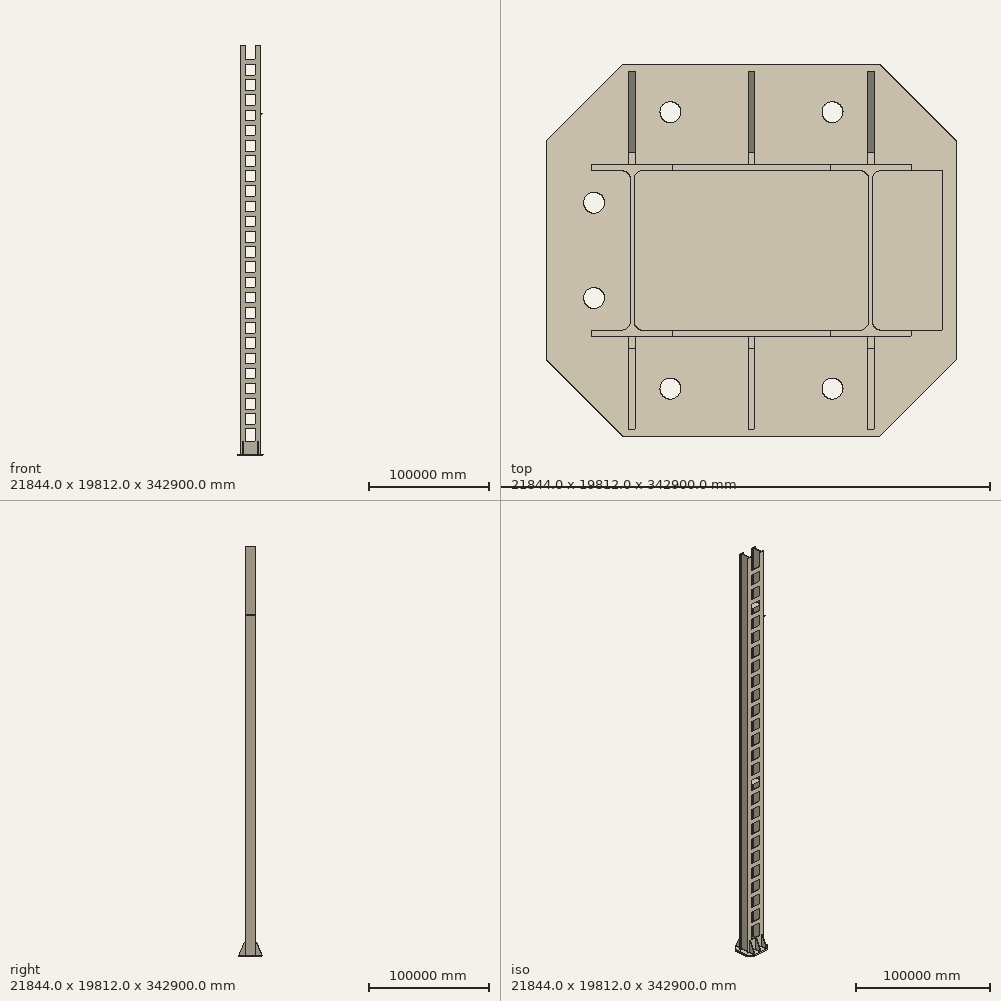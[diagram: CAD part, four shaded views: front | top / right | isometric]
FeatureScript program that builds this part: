
annotation { "Feature Type Name" : "Feature", "Feature Type Description" : "" }
export const myFeature = defineFeature(function(context is Context, id is Id, definition is map)
    precondition{}
    {
        {
            var Q0;
            Q0=qCreatedBy(makeId("Top.planeOp"),FACE);
            var sketch = newSketch(context, id + "F0", { "sketchPlane" : qUnion([Q0])});
            skLineSegment(sketch, "E0", {"start": v(-8509, 4572) * mm, "end": v(8509, 4572) * mm});
            skLineSegment(sketch, "E1", {"start": v(8509, 4572) * mm, "end": v(8509, 4249.42) * mm});
            skLineSegment(sketch, "E2", {"start": v(8509, 4249.42) * mm, "end": v(6908.8, 4249.42) * mm});
            skLineSegment(sketch, "E3", {"start": v(6451.6, 3792.22) * mm, "end": v(6451.6, -3792.22) * mm});
            skLineSegment(sketch, "E4", {"start": v(6908.8, -4249.42) * mm, "end": v(8509, -4249.42) * mm});
            skLineSegment(sketch, "E5", {"start": v(8509, -4249.42) * mm, "end": v(8509, -4572) * mm});
            skLineSegment(sketch, "E6", {"start": v(8509, -4572) * mm, "end": v(-8509, -4572) * mm});
            skLineSegment(sketch, "E7", {"start": v(-8509, -4572) * mm, "end": v(-8509, -4249.42) * mm});
            skLineSegment(sketch, "E8", {"start": v(-8509, -4249.42) * mm, "end": v(-6908.8, -4249.42) * mm});
            skLineSegment(sketch, "E9", {"start": v(-6451.6, -3792.22) * mm, "end": v(-6451.6, 3792.22) * mm});
            skLineSegment(sketch, "E10", {"start": v(-6908.8, 4249.42) * mm, "end": v(-8509, 4249.42) * mm});
            skLineSegment(sketch, "E11", {"start": v(-8509, 4249.42) * mm, "end": v(-8509, 4572) * mm});
            skPoint(sketch, "E12.visualSharp", {"position": v(-6451.6, 4249.42) * mm});
            skArc(sketch, "E12.filletArc", {"start": v(-6451.6, 3792.22) * mm, "mid": v(-6585.51, 4115.5) * mm, "end": v(-6908.8, 4249.42) * mm});
            skPoint(sketch, "E13.visualSharp", {"position": v(6451.6, 4249.42) * mm});
            skArc(sketch, "E13.filletArc", {"start": v(6908.8, 4249.42) * mm, "mid": v(6585.51, 4115.5) * mm, "end": v(6451.6, 3792.22) * mm});
            skPoint(sketch, "E14.visualSharp", {"position": v(6451.6, -4249.42) * mm});
            skArc(sketch, "E14.filletArc", {"start": v(6451.6, -3792.22) * mm, "mid": v(6585.51, -4115.5) * mm, "end": v(6908.8, -4249.42) * mm});
            skPoint(sketch, "E15.visualSharp", {"position": v(-6451.6, -4249.42) * mm});
            skArc(sketch, "E15.filletArc", {"start": v(-6908.8, -4249.42) * mm, "mid": v(-6585.51, -4115.5) * mm, "end": v(-6451.6, -3792.22) * mm});
            skSolve(sketch);
        }
        {
            var Q0;
            Q0=qSketchRegion(id+"F0",true);
            extrude(context, id + "F1", {"entities" : qUnion([Q0]), "depth" : 342900 * mm});
        }
        {
            var Q0;
            Q0=makeQuery(id+"F1.opExtrude","CAP_FACE",FACE,{"disambiguationData":[OSD([sQuery(id+"F0.wireOp",EDGE,"E0"),sQuery(id+"F0.wireOp",EDGE,"E1"),sQuery(id+"F0.wireOp",EDGE,"E2"),sQuery(id+"F0.wireOp",EDGE,"E3"),sQuery(id+"F0.wireOp",EDGE,"E4"),sQuery(id+"F0.wireOp",EDGE,"E5"),sQuery(id+"F0.wireOp",EDGE,"E6"),sQuery(id+"F0.wireOp",EDGE,"E7"),sQuery(id+"F0.wireOp",EDGE,"E8"),sQuery(id+"F0.wireOp",EDGE,"E9"),sQuery(id+"F0.wireOp",EDGE,"E10"),sQuery(id+"F0.wireOp",EDGE,"E11"),sQuery(id+"F0.wireOp",EDGE,"E12.filletArc"),sQuery(id+"F0.wireOp",EDGE,"E13.filletArc"),sQuery(id+"F0.wireOp",EDGE,"E14.filletArc"),sQuery(id+"F0.wireOp",EDGE,"E15.filletArc")])],"isStart":true});
            var sketch = newSketch(context, id + "F2", { "sketchPlane" : qUnion([Q0])});
            skLineSegment(sketch, "E16.bottom", {"start": v(-5791.2, 4249.42) * mm, "end": v(5791.2, 4249.42) * mm});
            skLineSegment(sketch, "E16.top", {"start": v(-5791.2, -4249.42) * mm, "end": v(5791.2, -4249.42) * mm});
            skLineSegment(sketch, "E16.left", {"start": v(-6248.4, 3792.22) * mm, "end": v(-6248.4, -3792.22) * mm});
            skLineSegment(sketch, "E16.right", {"start": v(6248.4, 3792.22) * mm, "end": v(6248.4, -3792.22) * mm});
            skPoint(sketch, "E17.visualSharp", {"position": v(-6248.4, 4249.42) * mm});
            skArc(sketch, "E17.filletArc", {"start": v(-5791.2, 4249.42) * mm, "mid": v(-6114.49, 4115.5) * mm, "end": v(-6248.4, 3792.22) * mm});
            skPoint(sketch, "E18.visualSharp", {"position": v(6248.4, 4249.42) * mm});
            skArc(sketch, "E18.filletArc", {"start": v(6248.4, 3792.22) * mm, "mid": v(6114.49, 4115.5) * mm, "end": v(5791.2, 4249.42) * mm});
            skPoint(sketch, "E19.visualSharp", {"position": v(6248.4, -4249.42) * mm});
            skArc(sketch, "E19.filletArc", {"start": v(5791.2, -4249.42) * mm, "mid": v(6114.49, -4115.5) * mm, "end": v(6248.4, -3792.22) * mm});
            skPoint(sketch, "E20.visualSharp", {"position": v(-6248.4, -4249.42) * mm});
            skArc(sketch, "E20.filletArc", {"start": v(-6248.4, -3792.22) * mm, "mid": v(-6114.49, -4115.5) * mm, "end": v(-5791.2, -4249.42) * mm});
            skLineSegment(sketch, "E21", {"start": v(-6913.3, 0) * mm, "end": v(6813.76, 0) * mm, "construction": true});
            skLineSegment(sketch, "E22", {"start": v(0, 5029.13) * mm, "end": v(0, -5231.93) * mm, "construction": true});
            skSolve(sketch);
        }
        {
            var Q0;
            Q0=qSketchRegion(id+"F2",true);
            extrude(context, id + "F3", {"entities" : qUnion([Q0]), "operationType" : NewBodyOperationType.REMOVE, "endBound" : BoundingType.THROUGH_ALL, "oppositeDirection" : true, "depth" : 25.4 * mm});
        }
        {
            var Q0;
            Q0=makeQuery(id+"F1.opExtrude","SWEPT_FACE",FACE,{"disambiguationData":[OSD([sQuery(id+"F0.wireOp",EDGE,"E6")])]});
            var sketch = newSketch(context, id + "F4", { "sketchPlane" : qUnion([Q0])});
            skLineSegment(sketch, "E23.bottom", {"start": v(-4191, 34925) * mm, "end": v(4191, 34925) * mm});
            skLineSegment(sketch, "E23.top", {"start": v(-4191, 26035) * mm, "end": v(4191, 26035) * mm});
            skLineSegment(sketch, "E23.left", {"start": v(-4191, 34925) * mm, "end": v(-4191, 26035) * mm});
            skLineSegment(sketch, "E23.right", {"start": v(4191, 34925) * mm, "end": v(4191, 26035) * mm});
            skLineSegment(sketch, "E24", {"start": v(0, -2627.58) * mm, "end": v(0, 406140.36) * mm, "construction": true});
            skLineSegment(sketch, "E25.0.1.0", {"start": v(-4191, 47625) * mm, "end": v(4191, 47625) * mm});
            skLineSegment(sketch, "E25.0.1.1", {"start": v(-4191, 38735) * mm, "end": v(4191, 38735) * mm});
            skLineSegment(sketch, "E25.0.1.2", {"start": v(-4191, 47625) * mm, "end": v(-4191, 38735) * mm});
            skLineSegment(sketch, "E25.0.1.3", {"start": v(4191, 47625) * mm, "end": v(4191, 38735) * mm});
            skLineSegment(sketch, "E25.0.2.0", {"start": v(-4191, 60325) * mm, "end": v(4191, 60325) * mm});
            skLineSegment(sketch, "E25.0.2.1", {"start": v(-4191, 51435) * mm, "end": v(4191, 51435) * mm});
            skLineSegment(sketch, "E25.0.2.2", {"start": v(-4191, 60325) * mm, "end": v(-4191, 51435) * mm});
            skLineSegment(sketch, "E25.0.2.3", {"start": v(4191, 60325) * mm, "end": v(4191, 51435) * mm});
            skLineSegment(sketch, "E25.0.3.0", {"start": v(-4191, 73025) * mm, "end": v(4191, 73025) * mm});
            skLineSegment(sketch, "E25.0.3.1", {"start": v(-4191, 64135) * mm, "end": v(4191, 64135) * mm});
            skLineSegment(sketch, "E25.0.3.2", {"start": v(-4191, 73025) * mm, "end": v(-4191, 64135) * mm});
            skLineSegment(sketch, "E25.0.3.3", {"start": v(4191, 73025) * mm, "end": v(4191, 64135) * mm});
            skLineSegment(sketch, "E25.0.4.0", {"start": v(-4191, 85725) * mm, "end": v(4191, 85725) * mm});
            skLineSegment(sketch, "E25.0.4.1", {"start": v(-4191, 76835) * mm, "end": v(4191, 76835) * mm});
            skLineSegment(sketch, "E25.0.4.2", {"start": v(-4191, 85725) * mm, "end": v(-4191, 76835) * mm});
            skLineSegment(sketch, "E25.0.4.3", {"start": v(4191, 85725) * mm, "end": v(4191, 76835) * mm});
            skLineSegment(sketch, "E25.0.5.0", {"start": v(-4191, 98425) * mm, "end": v(4191, 98425) * mm});
            skLineSegment(sketch, "E25.0.5.1", {"start": v(-4191, 89535) * mm, "end": v(4191, 89535) * mm});
            skLineSegment(sketch, "E25.0.5.2", {"start": v(-4191, 98425) * mm, "end": v(-4191, 89535) * mm});
            skLineSegment(sketch, "E25.0.5.3", {"start": v(4191, 98425) * mm, "end": v(4191, 89535) * mm});
            skLineSegment(sketch, "E25.0.6.0", {"start": v(-4191, 111125) * mm, "end": v(4191, 111125) * mm});
            skLineSegment(sketch, "E25.0.6.1", {"start": v(-4191, 102235) * mm, "end": v(4191, 102235) * mm});
            skLineSegment(sketch, "E25.0.6.2", {"start": v(-4191, 111125) * mm, "end": v(-4191, 102235) * mm});
            skLineSegment(sketch, "E25.0.6.3", {"start": v(4191, 111125) * mm, "end": v(4191, 102235) * mm});
            skLineSegment(sketch, "E25.0.7.0", {"start": v(-4191, 123825) * mm, "end": v(4191, 123825) * mm});
            skLineSegment(sketch, "E25.0.7.1", {"start": v(-4191, 114935) * mm, "end": v(4191, 114935) * mm});
            skLineSegment(sketch, "E25.0.7.2", {"start": v(-4191, 123825) * mm, "end": v(-4191, 114935) * mm});
            skLineSegment(sketch, "E25.0.7.3", {"start": v(4191, 123825) * mm, "end": v(4191, 114935) * mm});
            skLineSegment(sketch, "E25.0.8.0", {"start": v(-4191, 136525) * mm, "end": v(4191, 136525) * mm});
            skLineSegment(sketch, "E25.0.8.1", {"start": v(-4191, 127635) * mm, "end": v(4191, 127635) * mm});
            skLineSegment(sketch, "E25.0.8.2", {"start": v(-4191, 136525) * mm, "end": v(-4191, 127635) * mm});
            skLineSegment(sketch, "E25.0.8.3", {"start": v(4191, 136525) * mm, "end": v(4191, 127635) * mm});
            skLineSegment(sketch, "E25.0.9.0", {"start": v(-4191, 149225) * mm, "end": v(4191, 149225) * mm});
            skLineSegment(sketch, "E25.0.9.1", {"start": v(-4191, 140335) * mm, "end": v(4191, 140335) * mm});
            skLineSegment(sketch, "E25.0.9.2", {"start": v(-4191, 149225) * mm, "end": v(-4191, 140335) * mm});
            skLineSegment(sketch, "E25.0.9.3", {"start": v(4191, 149225) * mm, "end": v(4191, 140335) * mm});
            skLineSegment(sketch, "E25.0.10.0", {"start": v(-4191, 161925) * mm, "end": v(4191, 161925) * mm});
            skLineSegment(sketch, "E25.0.10.1", {"start": v(-4191, 153035) * mm, "end": v(4191, 153035) * mm});
            skLineSegment(sketch, "E25.0.10.2", {"start": v(-4191, 161925) * mm, "end": v(-4191, 153035) * mm});
            skLineSegment(sketch, "E25.0.10.3", {"start": v(4191, 161925) * mm, "end": v(4191, 153035) * mm});
            skLineSegment(sketch, "E25.0.11.0", {"start": v(-4191, 174625) * mm, "end": v(4191, 174625) * mm});
            skLineSegment(sketch, "E25.0.11.1", {"start": v(-4191, 165735) * mm, "end": v(4191, 165735) * mm});
            skLineSegment(sketch, "E25.0.11.2", {"start": v(-4191, 174625) * mm, "end": v(-4191, 165735) * mm});
            skLineSegment(sketch, "E25.0.11.3", {"start": v(4191, 174625) * mm, "end": v(4191, 165735) * mm});
            skLineSegment(sketch, "E25.0.12.0", {"start": v(-4191, 187325) * mm, "end": v(4191, 187325) * mm});
            skLineSegment(sketch, "E25.0.12.1", {"start": v(-4191, 178435) * mm, "end": v(4191, 178435) * mm});
            skLineSegment(sketch, "E25.0.12.2", {"start": v(-4191, 187325) * mm, "end": v(-4191, 178435) * mm});
            skLineSegment(sketch, "E25.0.12.3", {"start": v(4191, 187325) * mm, "end": v(4191, 178435) * mm});
            skLineSegment(sketch, "E25.0.13.0", {"start": v(-4191, 200025) * mm, "end": v(4191, 200025) * mm});
            skLineSegment(sketch, "E25.0.13.1", {"start": v(-4191, 191135) * mm, "end": v(4191, 191135) * mm});
            skLineSegment(sketch, "E25.0.13.2", {"start": v(-4191, 200025) * mm, "end": v(-4191, 191135) * mm});
            skLineSegment(sketch, "E25.0.13.3", {"start": v(4191, 200025) * mm, "end": v(4191, 191135) * mm});
            skLineSegment(sketch, "E25.0.14.0", {"start": v(-4191, 212725) * mm, "end": v(4191, 212725) * mm});
            skLineSegment(sketch, "E25.0.14.1", {"start": v(-4191, 203835) * mm, "end": v(4191, 203835) * mm});
            skLineSegment(sketch, "E25.0.14.2", {"start": v(-4191, 212725) * mm, "end": v(-4191, 203835) * mm});
            skLineSegment(sketch, "E25.0.14.3", {"start": v(4191, 212725) * mm, "end": v(4191, 203835) * mm});
            skLineSegment(sketch, "E25.0.15.0", {"start": v(-4191, 225425) * mm, "end": v(4191, 225425) * mm});
            skLineSegment(sketch, "E25.0.15.1", {"start": v(-4191, 216535) * mm, "end": v(4191, 216535) * mm});
            skLineSegment(sketch, "E25.0.15.2", {"start": v(-4191, 225425) * mm, "end": v(-4191, 216535) * mm});
            skLineSegment(sketch, "E25.0.15.3", {"start": v(4191, 225425) * mm, "end": v(4191, 216535) * mm});
            skLineSegment(sketch, "E25.0.16.0", {"start": v(-4191, 238125) * mm, "end": v(4191, 238125) * mm});
            skLineSegment(sketch, "E25.0.16.1", {"start": v(-4191, 229235) * mm, "end": v(4191, 229235) * mm});
            skLineSegment(sketch, "E25.0.16.2", {"start": v(-4191, 238125) * mm, "end": v(-4191, 229235) * mm});
            skLineSegment(sketch, "E25.0.16.3", {"start": v(4191, 238125) * mm, "end": v(4191, 229235) * mm});
            skLineSegment(sketch, "E25.0.17.0", {"start": v(-4191, 250825) * mm, "end": v(4191, 250825) * mm});
            skLineSegment(sketch, "E25.0.17.1", {"start": v(-4191, 241935) * mm, "end": v(4191, 241935) * mm});
            skLineSegment(sketch, "E25.0.17.2", {"start": v(-4191, 250825) * mm, "end": v(-4191, 241935) * mm});
            skLineSegment(sketch, "E25.0.17.3", {"start": v(4191, 250825) * mm, "end": v(4191, 241935) * mm});
            skLineSegment(sketch, "E25.0.18.0", {"start": v(-4191, 263525) * mm, "end": v(4191, 263525) * mm});
            skLineSegment(sketch, "E25.0.18.1", {"start": v(-4191, 254635) * mm, "end": v(4191, 254635) * mm});
            skLineSegment(sketch, "E25.0.18.2", {"start": v(-4191, 263525) * mm, "end": v(-4191, 254635) * mm});
            skLineSegment(sketch, "E25.0.18.3", {"start": v(4191, 263525) * mm, "end": v(4191, 254635) * mm});
            skLineSegment(sketch, "E25.0.19.0", {"start": v(-4191, 276225) * mm, "end": v(4191, 276225) * mm});
            skLineSegment(sketch, "E25.0.19.1", {"start": v(-4191, 267335) * mm, "end": v(4191, 267335) * mm});
            skLineSegment(sketch, "E25.0.19.2", {"start": v(-4191, 276225) * mm, "end": v(-4191, 267335) * mm});
            skLineSegment(sketch, "E25.0.19.3", {"start": v(4191, 276225) * mm, "end": v(4191, 267335) * mm});
            skLineSegment(sketch, "E25.0.20.0", {"start": v(-4191, 288925) * mm, "end": v(4191, 288925) * mm});
            skLineSegment(sketch, "E25.0.20.1", {"start": v(-4191, 280035) * mm, "end": v(4191, 280035) * mm});
            skLineSegment(sketch, "E25.0.20.2", {"start": v(-4191, 288925) * mm, "end": v(-4191, 280035) * mm});
            skLineSegment(sketch, "E25.0.20.3", {"start": v(4191, 288925) * mm, "end": v(4191, 280035) * mm});
            skLineSegment(sketch, "E25.0.21.0", {"start": v(-4191, 301625) * mm, "end": v(4191, 301625) * mm});
            skLineSegment(sketch, "E25.0.21.1", {"start": v(-4191, 292735) * mm, "end": v(4191, 292735) * mm});
            skLineSegment(sketch, "E25.0.21.2", {"start": v(-4191, 301625) * mm, "end": v(-4191, 292735) * mm});
            skLineSegment(sketch, "E25.0.21.3", {"start": v(4191, 301625) * mm, "end": v(4191, 292735) * mm});
            skLineSegment(sketch, "E25.0.22.0", {"start": v(-4191, 314325) * mm, "end": v(4191, 314325) * mm});
            skLineSegment(sketch, "E25.0.22.1", {"start": v(-4191, 305435) * mm, "end": v(4191, 305435) * mm});
            skLineSegment(sketch, "E25.0.22.2", {"start": v(-4191, 314325) * mm, "end": v(-4191, 305435) * mm});
            skLineSegment(sketch, "E25.0.22.3", {"start": v(4191, 314325) * mm, "end": v(4191, 305435) * mm});
            skLineSegment(sketch, "E25.0.23.0", {"start": v(-4191, 327025) * mm, "end": v(4191, 327025) * mm});
            skLineSegment(sketch, "E25.0.23.1", {"start": v(-4191, 318135) * mm, "end": v(4191, 318135) * mm});
            skLineSegment(sketch, "E25.0.23.2", {"start": v(-4191, 327025) * mm, "end": v(-4191, 318135) * mm});
            skLineSegment(sketch, "E25.0.23.3", {"start": v(4191, 327025) * mm, "end": v(4191, 318135) * mm});
            skLineSegment(sketch, "E25.1.1.0", {"start": v(-4191, 47625) * mm, "end": v(4191, 47625) * mm});
            skLineSegment(sketch, "E25.1.1.1", {"start": v(-4191, 38735) * mm, "end": v(4191, 38735) * mm});
            skLineSegment(sketch, "E25.1.1.2", {"start": v(-4191, 47625) * mm, "end": v(-4191, 38735) * mm});
            skLineSegment(sketch, "E25.1.1.3", {"start": v(4191, 47625) * mm, "end": v(4191, 38735) * mm});
            skLineSegment(sketch, "E25.1.2.0", {"start": v(-4191, 60325) * mm, "end": v(4191, 60325) * mm});
            skLineSegment(sketch, "E25.1.2.1", {"start": v(-4191, 51435) * mm, "end": v(4191, 51435) * mm});
            skLineSegment(sketch, "E25.1.2.2", {"start": v(-4191, 60325) * mm, "end": v(-4191, 51435) * mm});
            skLineSegment(sketch, "E25.1.2.3", {"start": v(4191, 60325) * mm, "end": v(4191, 51435) * mm});
            skLineSegment(sketch, "E25.1.3.0", {"start": v(-4191, 73025) * mm, "end": v(4191, 73025) * mm});
            skLineSegment(sketch, "E25.1.3.1", {"start": v(-4191, 64135) * mm, "end": v(4191, 64135) * mm});
            skLineSegment(sketch, "E25.1.3.2", {"start": v(-4191, 73025) * mm, "end": v(-4191, 64135) * mm});
            skLineSegment(sketch, "E25.1.3.3", {"start": v(4191, 73025) * mm, "end": v(4191, 64135) * mm});
            skLineSegment(sketch, "E25.1.4.0", {"start": v(-4191, 85725) * mm, "end": v(4191, 85725) * mm});
            skLineSegment(sketch, "E25.1.4.1", {"start": v(-4191, 76835) * mm, "end": v(4191, 76835) * mm});
            skLineSegment(sketch, "E25.1.4.2", {"start": v(-4191, 85725) * mm, "end": v(-4191, 76835) * mm});
            skLineSegment(sketch, "E25.1.4.3", {"start": v(4191, 85725) * mm, "end": v(4191, 76835) * mm});
            skLineSegment(sketch, "E25.1.5.0", {"start": v(-4191, 98425) * mm, "end": v(4191, 98425) * mm});
            skLineSegment(sketch, "E25.1.5.1", {"start": v(-4191, 89535) * mm, "end": v(4191, 89535) * mm});
            skLineSegment(sketch, "E25.1.5.2", {"start": v(-4191, 98425) * mm, "end": v(-4191, 89535) * mm});
            skLineSegment(sketch, "E25.1.5.3", {"start": v(4191, 98425) * mm, "end": v(4191, 89535) * mm});
            skLineSegment(sketch, "E25.1.6.0", {"start": v(-4191, 111125) * mm, "end": v(4191, 111125) * mm});
            skLineSegment(sketch, "E25.1.6.1", {"start": v(-4191, 102235) * mm, "end": v(4191, 102235) * mm});
            skLineSegment(sketch, "E25.1.6.2", {"start": v(-4191, 111125) * mm, "end": v(-4191, 102235) * mm});
            skLineSegment(sketch, "E25.1.6.3", {"start": v(4191, 111125) * mm, "end": v(4191, 102235) * mm});
            skLineSegment(sketch, "E25.1.7.0", {"start": v(-4191, 123825) * mm, "end": v(4191, 123825) * mm});
            skLineSegment(sketch, "E25.1.7.1", {"start": v(-4191, 114935) * mm, "end": v(4191, 114935) * mm});
            skLineSegment(sketch, "E25.1.7.2", {"start": v(-4191, 123825) * mm, "end": v(-4191, 114935) * mm});
            skLineSegment(sketch, "E25.1.7.3", {"start": v(4191, 123825) * mm, "end": v(4191, 114935) * mm});
            skLineSegment(sketch, "E25.1.8.0", {"start": v(-4191, 136525) * mm, "end": v(4191, 136525) * mm});
            skLineSegment(sketch, "E25.1.8.1", {"start": v(-4191, 127635) * mm, "end": v(4191, 127635) * mm});
            skLineSegment(sketch, "E25.1.8.2", {"start": v(-4191, 136525) * mm, "end": v(-4191, 127635) * mm});
            skLineSegment(sketch, "E25.1.8.3", {"start": v(4191, 136525) * mm, "end": v(4191, 127635) * mm});
            skLineSegment(sketch, "E25.1.9.0", {"start": v(-4191, 149225) * mm, "end": v(4191, 149225) * mm});
            skLineSegment(sketch, "E25.1.9.1", {"start": v(-4191, 140335) * mm, "end": v(4191, 140335) * mm});
            skLineSegment(sketch, "E25.1.9.2", {"start": v(-4191, 149225) * mm, "end": v(-4191, 140335) * mm});
            skLineSegment(sketch, "E25.1.9.3", {"start": v(4191, 149225) * mm, "end": v(4191, 140335) * mm});
            skLineSegment(sketch, "E25.1.10.0", {"start": v(-4191, 161925) * mm, "end": v(4191, 161925) * mm});
            skLineSegment(sketch, "E25.1.10.1", {"start": v(-4191, 153035) * mm, "end": v(4191, 153035) * mm});
            skLineSegment(sketch, "E25.1.10.2", {"start": v(-4191, 161925) * mm, "end": v(-4191, 153035) * mm});
            skLineSegment(sketch, "E25.1.10.3", {"start": v(4191, 161925) * mm, "end": v(4191, 153035) * mm});
            skLineSegment(sketch, "E25.1.11.0", {"start": v(-4191, 174625) * mm, "end": v(4191, 174625) * mm});
            skLineSegment(sketch, "E25.1.11.1", {"start": v(-4191, 165735) * mm, "end": v(4191, 165735) * mm});
            skLineSegment(sketch, "E25.1.11.2", {"start": v(-4191, 174625) * mm, "end": v(-4191, 165735) * mm});
            skLineSegment(sketch, "E25.1.11.3", {"start": v(4191, 174625) * mm, "end": v(4191, 165735) * mm});
            skLineSegment(sketch, "E25.1.12.0", {"start": v(-4191, 187325) * mm, "end": v(4191, 187325) * mm});
            skLineSegment(sketch, "E25.1.12.1", {"start": v(-4191, 178435) * mm, "end": v(4191, 178435) * mm});
            skLineSegment(sketch, "E25.1.12.2", {"start": v(-4191, 187325) * mm, "end": v(-4191, 178435) * mm});
            skLineSegment(sketch, "E25.1.12.3", {"start": v(4191, 187325) * mm, "end": v(4191, 178435) * mm});
            skLineSegment(sketch, "E25.1.13.0", {"start": v(-4191, 200025) * mm, "end": v(4191, 200025) * mm});
            skLineSegment(sketch, "E25.1.13.1", {"start": v(-4191, 191135) * mm, "end": v(4191, 191135) * mm});
            skLineSegment(sketch, "E25.1.13.2", {"start": v(-4191, 200025) * mm, "end": v(-4191, 191135) * mm});
            skLineSegment(sketch, "E25.1.13.3", {"start": v(4191, 200025) * mm, "end": v(4191, 191135) * mm});
            skLineSegment(sketch, "E25.1.14.0", {"start": v(-4191, 212725) * mm, "end": v(4191, 212725) * mm});
            skLineSegment(sketch, "E25.1.14.1", {"start": v(-4191, 203835) * mm, "end": v(4191, 203835) * mm});
            skLineSegment(sketch, "E25.1.14.2", {"start": v(-4191, 212725) * mm, "end": v(-4191, 203835) * mm});
            skLineSegment(sketch, "E25.1.14.3", {"start": v(4191, 212725) * mm, "end": v(4191, 203835) * mm});
            skLineSegment(sketch, "E25.1.15.0", {"start": v(-4191, 225425) * mm, "end": v(4191, 225425) * mm});
            skLineSegment(sketch, "E25.1.15.1", {"start": v(-4191, 216535) * mm, "end": v(4191, 216535) * mm});
            skLineSegment(sketch, "E25.1.15.2", {"start": v(-4191, 225425) * mm, "end": v(-4191, 216535) * mm});
            skLineSegment(sketch, "E25.1.15.3", {"start": v(4191, 225425) * mm, "end": v(4191, 216535) * mm});
            skLineSegment(sketch, "E25.1.16.0", {"start": v(-4191, 238125) * mm, "end": v(4191, 238125) * mm});
            skLineSegment(sketch, "E25.1.16.1", {"start": v(-4191, 229235) * mm, "end": v(4191, 229235) * mm});
            skLineSegment(sketch, "E25.1.16.2", {"start": v(-4191, 238125) * mm, "end": v(-4191, 229235) * mm});
            skLineSegment(sketch, "E25.1.16.3", {"start": v(4191, 238125) * mm, "end": v(4191, 229235) * mm});
            skLineSegment(sketch, "E25.1.17.0", {"start": v(-4191, 250825) * mm, "end": v(4191, 250825) * mm});
            skLineSegment(sketch, "E25.1.17.1", {"start": v(-4191, 241935) * mm, "end": v(4191, 241935) * mm});
            skLineSegment(sketch, "E25.1.17.2", {"start": v(-4191, 250825) * mm, "end": v(-4191, 241935) * mm});
            skLineSegment(sketch, "E25.1.17.3", {"start": v(4191, 250825) * mm, "end": v(4191, 241935) * mm});
            skLineSegment(sketch, "E25.1.18.0", {"start": v(-4191, 263525) * mm, "end": v(4191, 263525) * mm});
            skLineSegment(sketch, "E25.1.18.1", {"start": v(-4191, 254635) * mm, "end": v(4191, 254635) * mm});
            skLineSegment(sketch, "E25.1.18.2", {"start": v(-4191, 263525) * mm, "end": v(-4191, 254635) * mm});
            skLineSegment(sketch, "E25.1.18.3", {"start": v(4191, 263525) * mm, "end": v(4191, 254635) * mm});
            skLineSegment(sketch, "E25.1.19.0", {"start": v(-4191, 276225) * mm, "end": v(4191, 276225) * mm});
            skLineSegment(sketch, "E25.1.19.1", {"start": v(-4191, 267335) * mm, "end": v(4191, 267335) * mm});
            skLineSegment(sketch, "E25.1.19.2", {"start": v(-4191, 276225) * mm, "end": v(-4191, 267335) * mm});
            skLineSegment(sketch, "E25.1.19.3", {"start": v(4191, 276225) * mm, "end": v(4191, 267335) * mm});
            skLineSegment(sketch, "E25.1.20.0", {"start": v(-4191, 288925) * mm, "end": v(4191, 288925) * mm});
            skLineSegment(sketch, "E25.1.20.1", {"start": v(-4191, 280035) * mm, "end": v(4191, 280035) * mm});
            skLineSegment(sketch, "E25.1.20.2", {"start": v(-4191, 288925) * mm, "end": v(-4191, 280035) * mm});
            skLineSegment(sketch, "E25.1.20.3", {"start": v(4191, 288925) * mm, "end": v(4191, 280035) * mm});
            skLineSegment(sketch, "E25.1.21.0", {"start": v(-4191, 301625) * mm, "end": v(4191, 301625) * mm});
            skLineSegment(sketch, "E25.1.21.1", {"start": v(-4191, 292735) * mm, "end": v(4191, 292735) * mm});
            skLineSegment(sketch, "E25.1.21.2", {"start": v(-4191, 301625) * mm, "end": v(-4191, 292735) * mm});
            skLineSegment(sketch, "E25.1.21.3", {"start": v(4191, 301625) * mm, "end": v(4191, 292735) * mm});
            skLineSegment(sketch, "E25.1.22.0", {"start": v(-4191, 314325) * mm, "end": v(4191, 314325) * mm});
            skLineSegment(sketch, "E25.1.22.1", {"start": v(-4191, 305435) * mm, "end": v(4191, 305435) * mm});
            skLineSegment(sketch, "E25.1.22.2", {"start": v(-4191, 314325) * mm, "end": v(-4191, 305435) * mm});
            skLineSegment(sketch, "E25.1.22.3", {"start": v(4191, 314325) * mm, "end": v(4191, 305435) * mm});
            skLineSegment(sketch, "E25.1.23.0", {"start": v(-4191, 327025) * mm, "end": v(4191, 327025) * mm});
            skLineSegment(sketch, "E25.1.23.1", {"start": v(-4191, 318135) * mm, "end": v(4191, 318135) * mm});
            skLineSegment(sketch, "E25.1.23.2", {"start": v(-4191, 327025) * mm, "end": v(-4191, 318135) * mm});
            skLineSegment(sketch, "E25.1.23.3", {"start": v(4191, 327025) * mm, "end": v(4191, 318135) * mm});
            skLineSegment(sketch, "E25.2.1.0", {"start": v(-4191, 47625) * mm, "end": v(4191, 47625) * mm});
            skLineSegment(sketch, "E25.2.1.1", {"start": v(-4191, 38735) * mm, "end": v(4191, 38735) * mm});
            skLineSegment(sketch, "E25.2.1.2", {"start": v(-4191, 47625) * mm, "end": v(-4191, 38735) * mm});
            skLineSegment(sketch, "E25.2.1.3", {"start": v(4191, 47625) * mm, "end": v(4191, 38735) * mm});
            skLineSegment(sketch, "E25.2.2.0", {"start": v(-4191, 60325) * mm, "end": v(4191, 60325) * mm});
            skLineSegment(sketch, "E25.2.2.1", {"start": v(-4191, 51435) * mm, "end": v(4191, 51435) * mm});
            skLineSegment(sketch, "E25.2.2.2", {"start": v(-4191, 60325) * mm, "end": v(-4191, 51435) * mm});
            skLineSegment(sketch, "E25.2.2.3", {"start": v(4191, 60325) * mm, "end": v(4191, 51435) * mm});
            skLineSegment(sketch, "E25.2.3.0", {"start": v(-4191, 73025) * mm, "end": v(4191, 73025) * mm});
            skLineSegment(sketch, "E25.2.3.1", {"start": v(-4191, 64135) * mm, "end": v(4191, 64135) * mm});
            skLineSegment(sketch, "E25.2.3.2", {"start": v(-4191, 73025) * mm, "end": v(-4191, 64135) * mm});
            skLineSegment(sketch, "E25.2.3.3", {"start": v(4191, 73025) * mm, "end": v(4191, 64135) * mm});
            skLineSegment(sketch, "E25.2.4.0", {"start": v(-4191, 85725) * mm, "end": v(4191, 85725) * mm});
            skLineSegment(sketch, "E25.2.4.1", {"start": v(-4191, 76835) * mm, "end": v(4191, 76835) * mm});
            skLineSegment(sketch, "E25.2.4.2", {"start": v(-4191, 85725) * mm, "end": v(-4191, 76835) * mm});
            skLineSegment(sketch, "E25.2.4.3", {"start": v(4191, 85725) * mm, "end": v(4191, 76835) * mm});
            skLineSegment(sketch, "E25.2.5.0", {"start": v(-4191, 98425) * mm, "end": v(4191, 98425) * mm});
            skLineSegment(sketch, "E25.2.5.1", {"start": v(-4191, 89535) * mm, "end": v(4191, 89535) * mm});
            skLineSegment(sketch, "E25.2.5.2", {"start": v(-4191, 98425) * mm, "end": v(-4191, 89535) * mm});
            skLineSegment(sketch, "E25.2.5.3", {"start": v(4191, 98425) * mm, "end": v(4191, 89535) * mm});
            skLineSegment(sketch, "E25.2.6.0", {"start": v(-4191, 111125) * mm, "end": v(4191, 111125) * mm});
            skLineSegment(sketch, "E25.2.6.1", {"start": v(-4191, 102235) * mm, "end": v(4191, 102235) * mm});
            skLineSegment(sketch, "E25.2.6.2", {"start": v(-4191, 111125) * mm, "end": v(-4191, 102235) * mm});
            skLineSegment(sketch, "E25.2.6.3", {"start": v(4191, 111125) * mm, "end": v(4191, 102235) * mm});
            skLineSegment(sketch, "E25.2.7.0", {"start": v(-4191, 123825) * mm, "end": v(4191, 123825) * mm});
            skLineSegment(sketch, "E25.2.7.1", {"start": v(-4191, 114935) * mm, "end": v(4191, 114935) * mm});
            skLineSegment(sketch, "E25.2.7.2", {"start": v(-4191, 123825) * mm, "end": v(-4191, 114935) * mm});
            skLineSegment(sketch, "E25.2.7.3", {"start": v(4191, 123825) * mm, "end": v(4191, 114935) * mm});
            skLineSegment(sketch, "E25.2.8.0", {"start": v(-4191, 136525) * mm, "end": v(4191, 136525) * mm});
            skLineSegment(sketch, "E25.2.8.1", {"start": v(-4191, 127635) * mm, "end": v(4191, 127635) * mm});
            skLineSegment(sketch, "E25.2.8.2", {"start": v(-4191, 136525) * mm, "end": v(-4191, 127635) * mm});
            skLineSegment(sketch, "E25.2.8.3", {"start": v(4191, 136525) * mm, "end": v(4191, 127635) * mm});
            skLineSegment(sketch, "E25.2.9.0", {"start": v(-4191, 149225) * mm, "end": v(4191, 149225) * mm});
            skLineSegment(sketch, "E25.2.9.1", {"start": v(-4191, 140335) * mm, "end": v(4191, 140335) * mm});
            skLineSegment(sketch, "E25.2.9.2", {"start": v(-4191, 149225) * mm, "end": v(-4191, 140335) * mm});
            skLineSegment(sketch, "E25.2.9.3", {"start": v(4191, 149225) * mm, "end": v(4191, 140335) * mm});
            skLineSegment(sketch, "E25.2.10.0", {"start": v(-4191, 161925) * mm, "end": v(4191, 161925) * mm});
            skLineSegment(sketch, "E25.2.10.1", {"start": v(-4191, 153035) * mm, "end": v(4191, 153035) * mm});
            skLineSegment(sketch, "E25.2.10.2", {"start": v(-4191, 161925) * mm, "end": v(-4191, 153035) * mm});
            skLineSegment(sketch, "E25.2.10.3", {"start": v(4191, 161925) * mm, "end": v(4191, 153035) * mm});
            skLineSegment(sketch, "E25.2.11.0", {"start": v(-4191, 174625) * mm, "end": v(4191, 174625) * mm});
            skLineSegment(sketch, "E25.2.11.1", {"start": v(-4191, 165735) * mm, "end": v(4191, 165735) * mm});
            skLineSegment(sketch, "E25.2.11.2", {"start": v(-4191, 174625) * mm, "end": v(-4191, 165735) * mm});
            skLineSegment(sketch, "E25.2.11.3", {"start": v(4191, 174625) * mm, "end": v(4191, 165735) * mm});
            skLineSegment(sketch, "E25.2.12.0", {"start": v(-4191, 187325) * mm, "end": v(4191, 187325) * mm});
            skLineSegment(sketch, "E25.2.12.1", {"start": v(-4191, 178435) * mm, "end": v(4191, 178435) * mm});
            skLineSegment(sketch, "E25.2.12.2", {"start": v(-4191, 187325) * mm, "end": v(-4191, 178435) * mm});
            skLineSegment(sketch, "E25.2.12.3", {"start": v(4191, 187325) * mm, "end": v(4191, 178435) * mm});
            skLineSegment(sketch, "E25.2.13.0", {"start": v(-4191, 200025) * mm, "end": v(4191, 200025) * mm});
            skLineSegment(sketch, "E25.2.13.1", {"start": v(-4191, 191135) * mm, "end": v(4191, 191135) * mm});
            skLineSegment(sketch, "E25.2.13.2", {"start": v(-4191, 200025) * mm, "end": v(-4191, 191135) * mm});
            skLineSegment(sketch, "E25.2.13.3", {"start": v(4191, 200025) * mm, "end": v(4191, 191135) * mm});
            skLineSegment(sketch, "E25.2.14.0", {"start": v(-4191, 212725) * mm, "end": v(4191, 212725) * mm});
            skLineSegment(sketch, "E25.2.14.1", {"start": v(-4191, 203835) * mm, "end": v(4191, 203835) * mm});
            skLineSegment(sketch, "E25.2.14.2", {"start": v(-4191, 212725) * mm, "end": v(-4191, 203835) * mm});
            skLineSegment(sketch, "E25.2.14.3", {"start": v(4191, 212725) * mm, "end": v(4191, 203835) * mm});
            skLineSegment(sketch, "E25.2.15.0", {"start": v(-4191, 225425) * mm, "end": v(4191, 225425) * mm});
            skLineSegment(sketch, "E25.2.15.1", {"start": v(-4191, 216535) * mm, "end": v(4191, 216535) * mm});
            skLineSegment(sketch, "E25.2.15.2", {"start": v(-4191, 225425) * mm, "end": v(-4191, 216535) * mm});
            skLineSegment(sketch, "E25.2.15.3", {"start": v(4191, 225425) * mm, "end": v(4191, 216535) * mm});
            skLineSegment(sketch, "E25.2.16.0", {"start": v(-4191, 238125) * mm, "end": v(4191, 238125) * mm});
            skLineSegment(sketch, "E25.2.16.1", {"start": v(-4191, 229235) * mm, "end": v(4191, 229235) * mm});
            skLineSegment(sketch, "E25.2.16.2", {"start": v(-4191, 238125) * mm, "end": v(-4191, 229235) * mm});
            skLineSegment(sketch, "E25.2.16.3", {"start": v(4191, 238125) * mm, "end": v(4191, 229235) * mm});
            skLineSegment(sketch, "E25.2.17.0", {"start": v(-4191, 250825) * mm, "end": v(4191, 250825) * mm});
            skLineSegment(sketch, "E25.2.17.1", {"start": v(-4191, 241935) * mm, "end": v(4191, 241935) * mm});
            skLineSegment(sketch, "E25.2.17.2", {"start": v(-4191, 250825) * mm, "end": v(-4191, 241935) * mm});
            skLineSegment(sketch, "E25.2.17.3", {"start": v(4191, 250825) * mm, "end": v(4191, 241935) * mm});
            skLineSegment(sketch, "E25.2.18.0", {"start": v(-4191, 263525) * mm, "end": v(4191, 263525) * mm});
            skLineSegment(sketch, "E25.2.18.1", {"start": v(-4191, 254635) * mm, "end": v(4191, 254635) * mm});
            skLineSegment(sketch, "E25.2.18.2", {"start": v(-4191, 263525) * mm, "end": v(-4191, 254635) * mm});
            skLineSegment(sketch, "E25.2.18.3", {"start": v(4191, 263525) * mm, "end": v(4191, 254635) * mm});
            skLineSegment(sketch, "E25.2.19.0", {"start": v(-4191, 276225) * mm, "end": v(4191, 276225) * mm});
            skLineSegment(sketch, "E25.2.19.1", {"start": v(-4191, 267335) * mm, "end": v(4191, 267335) * mm});
            skLineSegment(sketch, "E25.2.19.2", {"start": v(-4191, 276225) * mm, "end": v(-4191, 267335) * mm});
            skLineSegment(sketch, "E25.2.19.3", {"start": v(4191, 276225) * mm, "end": v(4191, 267335) * mm});
            skLineSegment(sketch, "E25.2.20.0", {"start": v(-4191, 288925) * mm, "end": v(4191, 288925) * mm});
            skLineSegment(sketch, "E25.2.20.1", {"start": v(-4191, 280035) * mm, "end": v(4191, 280035) * mm});
            skLineSegment(sketch, "E25.2.20.2", {"start": v(-4191, 288925) * mm, "end": v(-4191, 280035) * mm});
            skLineSegment(sketch, "E25.2.20.3", {"start": v(4191, 288925) * mm, "end": v(4191, 280035) * mm});
            skLineSegment(sketch, "E25.2.21.0", {"start": v(-4191, 301625) * mm, "end": v(4191, 301625) * mm});
            skLineSegment(sketch, "E25.2.21.1", {"start": v(-4191, 292735) * mm, "end": v(4191, 292735) * mm});
            skLineSegment(sketch, "E25.2.21.2", {"start": v(-4191, 301625) * mm, "end": v(-4191, 292735) * mm});
            skLineSegment(sketch, "E25.2.21.3", {"start": v(4191, 301625) * mm, "end": v(4191, 292735) * mm});
            skLineSegment(sketch, "E25.2.22.0", {"start": v(-4191, 314325) * mm, "end": v(4191, 314325) * mm});
            skLineSegment(sketch, "E25.2.22.1", {"start": v(-4191, 305435) * mm, "end": v(4191, 305435) * mm});
            skLineSegment(sketch, "E25.2.22.2", {"start": v(-4191, 314325) * mm, "end": v(-4191, 305435) * mm});
            skLineSegment(sketch, "E25.2.22.3", {"start": v(4191, 314325) * mm, "end": v(4191, 305435) * mm});
            skLineSegment(sketch, "E25.2.23.0", {"start": v(-4191, 327025) * mm, "end": v(4191, 327025) * mm});
            skLineSegment(sketch, "E25.2.23.1", {"start": v(-4191, 318135) * mm, "end": v(4191, 318135) * mm});
            skLineSegment(sketch, "E25.2.23.2", {"start": v(-4191, 327025) * mm, "end": v(-4191, 318135) * mm});
            skLineSegment(sketch, "E25.2.23.3", {"start": v(4191, 327025) * mm, "end": v(4191, 318135) * mm});
            skLineSegment(sketch, "E25.direction1", {"start": v(-4191, 26035) * mm, "end": v(-4191, 26035) * mm});
            skLineSegment(sketch, "E25.direction2", {"start": v(-4191, 26035) * mm, "end": v(-4191, 38735) * mm, "construction": true});
            skLineSegment(sketch, "E26.bottom", {"start": v(-4191, 342900) * mm, "end": v(4191, 342900) * mm});
            skLineSegment(sketch, "E26.top", {"start": v(-4191, 330835) * mm, "end": v(4191, 330835) * mm});
            skLineSegment(sketch, "E26.left", {"start": v(-4191, 342900) * mm, "end": v(-4191, 330835) * mm});
            skLineSegment(sketch, "E26.right", {"start": v(4191, 342900) * mm, "end": v(4191, 330835) * mm});
            skLineSegment(sketch, "E27.bottom", {"start": v(-4191, 22225) * mm, "end": v(4191, 22225) * mm});
            skLineSegment(sketch, "E27.top", {"start": v(-4191, 11303) * mm, "end": v(4191, 11303) * mm});
            skLineSegment(sketch, "E27.left", {"start": v(-4191, 22225) * mm, "end": v(-4191, 11303) * mm});
            skLineSegment(sketch, "E27.right", {"start": v(4191, 22225) * mm, "end": v(4191, 11303) * mm});
            skSolve(sketch);
        }
        {
            var Q0;
            Q0=qSketchRegion(id+"F4",true);
            extrude(context, id + "F5", {"entities" : qUnion([Q0]), "operationType" : NewBodyOperationType.REMOVE, "endBound" : BoundingType.THROUGH_ALL, "oppositeDirection" : true, "depth" : 25.4 * mm});
        }
        {
            var Q0;
            Q0=qCreatedBy(makeId("Top.planeOp"),FACE);
            cPlane(context, id + "F6", {"entities" : qUnion([Q0]), "cplaneType" : CPlaneType.OFFSET, "offset" : 144780 * mm, "width" : 152.4 * mm, "height" : 152.4 * mm});
        }
        {
            var Q0;
            Q0=qCreatedBy(id+"F6.planeOp",FACE);
            var sketch = newSketch(context, id + "F7", { "sketchPlane" : qUnion([Q0])});
            skLineSegment(sketch, "E28", {"start": v(0, 5038.5) * mm, "end": v(0, -5387.54) * mm, "construction": true});
            skLineSegment(sketch, "E29", {"start": v(-6816.57, 0) * mm, "end": v(7079.48, 0) * mm, "construction": true});
            skLineSegment(sketch, "E30.bottom", {"start": v(-5791.2, 4249.42) * mm, "end": v(5791.2, 4249.42) * mm});
            skLineSegment(sketch, "E30.top", {"start": v(-5791.2, -4249.42) * mm, "end": v(5791.2, -4249.42) * mm});
            skLineSegment(sketch, "E30.left", {"start": v(-6248.4, 3792.22) * mm, "end": v(-6248.4, -3792.22) * mm});
            skLineSegment(sketch, "E30.right", {"start": v(6248.4, 3792.22) * mm, "end": v(6248.4, -3792.22) * mm});
            skPoint(sketch, "E31.visualSharp", {"position": v(-6248.4, 4249.42) * mm});
            skArc(sketch, "E31.filletArc", {"start": v(-5791.2, 4249.42) * mm, "mid": v(-6114.49, 4115.5) * mm, "end": v(-6248.4, 3792.22) * mm});
            skPoint(sketch, "E32.visualSharp", {"position": v(6248.4, 4249.42) * mm});
            skArc(sketch, "E32.filletArc", {"start": v(6248.4, 3792.22) * mm, "mid": v(6114.49, 4115.5) * mm, "end": v(5791.2, 4249.42) * mm});
            skPoint(sketch, "E33.visualSharp", {"position": v(6248.4, -4249.42) * mm});
            skArc(sketch, "E33.filletArc", {"start": v(5791.2, -4249.42) * mm, "mid": v(6114.49, -4115.5) * mm, "end": v(6248.4, -3792.22) * mm});
            skPoint(sketch, "E34.visualSharp", {"position": v(-6248.4, -4249.42) * mm});
            skArc(sketch, "E34.filletArc", {"start": v(-6248.4, -3792.22) * mm, "mid": v(-6114.49, -4115.5) * mm, "end": v(-5791.2, -4249.42) * mm});
            skSolve(sketch);
        }
        {
            var Q0;
            Q0=qSketchRegion(id+"F7",true);
            extrude(context, id + "F8", {"entities" : qUnion([Q0]), "operationType" : NewBodyOperationType.ADD, "endBound" : BoundingType.SYMMETRIC, "depth" : 152.4 * mm});
        }
        {
            var Q0;
            Q0=qCreatedBy(makeId("Top.planeOp"),FACE);
            cPlane(context, id + "F9", {"entities" : qUnion([Q0]), "cplaneType" : CPlaneType.OFFSET, "offset" : 297180 * mm, "width" : 152.4 * mm, "height" : 152.4 * mm});
        }
        {
            var Q0;
            Q0=qCreatedBy(id+"F9.planeOp",FACE);
            var sketch = newSketch(context, id + "F10", { "sketchPlane" : qUnion([Q0])});
            skLineSegment(sketch, "E35.bottom", {"start": v(-5791.2, 4249.42) * mm, "end": v(5791.2, 4249.42) * mm});
            skLineSegment(sketch, "E35.top", {"start": v(-5791.2, -4249.42) * mm, "end": v(5791.2, -4249.42) * mm});
            skLineSegment(sketch, "E35.left", {"start": v(-6248.4, 3792.22) * mm, "end": v(-6248.4, -3792.22) * mm});
            skLineSegment(sketch, "E35.right", {"start": v(6248.4, 3792.22) * mm, "end": v(6248.4, -3792.22) * mm});
            skLineSegment(sketch, "E36", {"start": v(-6862.25, 0) * mm, "end": v(7060.04, 0) * mm, "construction": true});
            skLineSegment(sketch, "E37", {"start": v(0, 5227.84) * mm, "end": v(0, -5440.7) * mm, "construction": true});
            skPoint(sketch, "E38.visualSharp", {"position": v(-6248.4, 4249.42) * mm});
            skArc(sketch, "E38.filletArc", {"start": v(-5791.2, 4249.42) * mm, "mid": v(-6114.49, 4115.5) * mm, "end": v(-6248.4, 3792.22) * mm});
            skPoint(sketch, "E39.visualSharp", {"position": v(6248.4, 4249.42) * mm});
            skArc(sketch, "E39.filletArc", {"start": v(6248.4, 3792.22) * mm, "mid": v(6114.49, 4115.5) * mm, "end": v(5791.2, 4249.42) * mm});
            skPoint(sketch, "E40.visualSharp", {"position": v(6248.4, -4249.42) * mm});
            skArc(sketch, "E40.filletArc", {"start": v(5791.2, -4249.42) * mm, "mid": v(6114.49, -4115.5) * mm, "end": v(6248.4, -3792.22) * mm});
            skPoint(sketch, "E41.visualSharp", {"position": v(-6248.4, -4249.42) * mm});
            skArc(sketch, "E41.filletArc", {"start": v(-6248.4, -3792.22) * mm, "mid": v(-6114.49, -4115.5) * mm, "end": v(-5791.2, -4249.42) * mm});
            skSolve(sketch);
        }
        {
            var Q0;
            Q0=qSketchRegion(id+"F10",true);
            extrude(context, id + "F11", {"entities" : qUnion([Q0]), "operationType" : NewBodyOperationType.ADD, "endBound" : BoundingType.SYMMETRIC, "depth" : 152.4 * mm});
        }
        {
            var Q0;
            Q0=qCreatedBy(makeId("Right.planeOp"),FACE);
            var sketch = newSketch(context, id + "F12", { "sketchPlane" : qUnion([Q0])});
            skLineSegment(sketch, "E42", {"start": v(-9525, 0) * mm, "end": v(-9525, 1778) * mm});
            skLineSegment(sketch, "E43", {"start": v(-9525, 1778) * mm, "end": v(-5207, 11303) * mm});
            skLineSegment(sketch, "E44", {"start": v(-5207, 11303) * mm, "end": v(5207, 11303) * mm});
            skLineSegment(sketch, "E45", {"start": v(5207, 11303) * mm, "end": v(9525, 1778) * mm});
            skLineSegment(sketch, "E46", {"start": v(9525, 1778) * mm, "end": v(9525, 0) * mm});
            skLineSegment(sketch, "E47", {"start": v(9525, 0) * mm, "end": v(-9525, 0) * mm});
            skLineSegment(sketch, "E48", {"start": v(0, -2307.15) * mm, "end": v(0, 14569.66) * mm, "construction": true});
            skSolve(sketch);
        }
        {
            var Q0;
            Q0=qSketchRegion(id+"F12",true);
            extrude(context, id + "F13", {"entities" : qUnion([Q0]), "operationType" : NewBodyOperationType.ADD, "endBound" : BoundingType.SYMMETRIC, "depth" : 304.8 * mm});
        }
        {
            var Q0;
            Q0=qCreatedBy(makeId("Right.planeOp"),FACE);
            cPlane(context, id + "F14", {"entities" : qUnion([Q0]), "cplaneType" : CPlaneType.OFFSET, "offset" : 6350 * mm, "width" : 152.4 * mm, "height" : 152.4 * mm});
        }
        {
            var Q0;
            Q0=qCreatedBy(id+"F14.planeOp",FACE);
            var sketch = newSketch(context, id + "F15", { "sketchPlane" : qUnion([Q0])});
            skLineSegment(sketch, "E49", {"start": v(4572, 0) * mm, "end": v(4572, 11303) * mm});
            skLineSegment(sketch, "E50", {"start": v(4572, 11303) * mm, "end": v(5207, 11303) * mm});
            skLineSegment(sketch, "E51", {"start": v(5207, 11303) * mm, "end": v(9525, 1778) * mm});
            skLineSegment(sketch, "E52", {"start": v(9525, 1778) * mm, "end": v(9525, 0) * mm});
            skLineSegment(sketch, "E53", {"start": v(9525, 0) * mm, "end": v(4572, 0) * mm});
            skLineSegment(sketch, "E54", {"start": v(0, -1220.16) * mm, "end": v(0, 13301) * mm, "construction": true});
            skLineSegment(sketch, "E55.MirrorCS", {"start": v(-4572, 11303) * mm, "end": v(-5207, 11303) * mm});
            skLineSegment(sketch, "E56.MirrorCS", {"start": v(-4572, 0) * mm, "end": v(-4572, 11303) * mm});
            skLineSegment(sketch, "E57.MirrorCS", {"start": v(-5207, 11303) * mm, "end": v(-9525, 1778) * mm});
            skLineSegment(sketch, "E58.MirrorCS", {"start": v(-9525, 1778) * mm, "end": v(-9525, 0) * mm});
            skLineSegment(sketch, "E59.MirrorCS", {"start": v(-9525, 0) * mm, "end": v(-4572, 0) * mm});
            skSolve(sketch);
        }
        {
            var Q0;
            Q0=qSketchRegion(id+"F15",true);
            extrude(context, id + "F16", {"entities" : qUnion([Q0]), "operationType" : NewBodyOperationType.ADD, "endBound" : BoundingType.SYMMETRIC, "depth" : 355.6 * mm});
        }
        {
            var Q0;
            Q0=qCreatedBy(makeId("Right.planeOp"),FACE);
            cPlane(context, id + "F17", {"entities" : qUnion([Q0]), "cplaneType" : CPlaneType.OFFSET, "offset" : 6350 * mm, "oppositeDirection" : true, "width" : 152.4 * mm, "height" : 152.4 * mm});
        }
        {
            var Q0;
            Q0=qCreatedBy(id+"F17.planeOp",FACE);
            var sketch = newSketch(context, id + "F18", { "sketchPlane" : qUnion([Q0])});
            skLineSegment(sketch, "E60", {"start": v(4572, 0) * mm, "end": v(4572, 11303) * mm});
            skLineSegment(sketch, "E61", {"start": v(4572, 11303) * mm, "end": v(5207, 11303) * mm});
            skLineSegment(sketch, "E62", {"start": v(5207, 11303) * mm, "end": v(9525, 1778) * mm});
            skLineSegment(sketch, "E63", {"start": v(9525, 1778) * mm, "end": v(9525, 0) * mm});
            skLineSegment(sketch, "E64", {"start": v(9525, 0) * mm, "end": v(4572, 0) * mm});
            skLineSegment(sketch, "E65", {"start": v(0, -2703.1) * mm, "end": v(0, 13730.2) * mm, "construction": true});
            skLineSegment(sketch, "E66.MirrorCS", {"start": v(-4572, 11303) * mm, "end": v(-5207, 11303) * mm});
            skLineSegment(sketch, "E67.MirrorCS", {"start": v(-5207, 11303) * mm, "end": v(-9525, 1778) * mm});
            skLineSegment(sketch, "E68.MirrorCS", {"start": v(-4572, 0) * mm, "end": v(-4572, 11303) * mm});
            skLineSegment(sketch, "E69.MirrorCS", {"start": v(-9525, 1778) * mm, "end": v(-9525, 0) * mm});
            skLineSegment(sketch, "E70.MirrorCS", {"start": v(-9525, 0) * mm, "end": v(-4572, 0) * mm});
            skSolve(sketch);
        }
        {
            var Q0;
            Q0=qSketchRegion(id+"F18",true);
            extrude(context, id + "F19", {"entities" : qUnion([Q0]), "operationType" : NewBodyOperationType.ADD, "endBound" : BoundingType.SYMMETRIC, "depth" : 355.6 * mm});
        }
        {
            var Q0;
            Q0=qCreatedBy(makeId("Top.planeOp"),FACE);
            var sketch = newSketch(context, id + "F20", { "sketchPlane" : qUnion([Q0])});
            skLineSegment(sketch, "E71", {"start": v(-10922, -5842) * mm, "end": v(-10922, 5842) * mm});
            skLineSegment(sketch, "E72", {"start": v(-10922, 5842) * mm, "end": v(-6858, 9906) * mm});
            skLineSegment(sketch, "E73", {"start": v(-6858, 9906) * mm, "end": v(6858, 9906) * mm});
            skLineSegment(sketch, "E74", {"start": v(6858, 9906) * mm, "end": v(10922, 5842) * mm});
            skLineSegment(sketch, "E75", {"start": v(10922, 5842) * mm, "end": v(10922, -5842) * mm});
            skLineSegment(sketch, "E76", {"start": v(10922, -5842) * mm, "end": v(6858, -9906) * mm});
            skLineSegment(sketch, "E77", {"start": v(6858, -9906) * mm, "end": v(-6858, -9906) * mm});
            skLineSegment(sketch, "E78", {"start": v(-6858, -9906) * mm, "end": v(-10922, -5842) * mm});
            skLineSegment(sketch, "E79", {"start": v(0, 11047.18) * mm, "end": v(0, -11914.8) * mm, "construction": true});
            skLineSegment(sketch, "E80", {"start": v(-11304.08, 0) * mm, "end": v(12211.2, 0) * mm, "construction": true});
            skCircle(sketch, "E81", {"center": v(4318, 7366) * mm, "radius": 558.8 * mm});
            skCircle(sketch, "E82", {"center": v(8382, 2540) * mm, "radius": 558.8 * mm});
            skCircle(sketch, "E83.MirrorC", {"center": v(4318, -7366) * mm, "radius": 558.8 * mm});
            skCircle(sketch, "E84.MirrorC", {"center": v(8382, -2540) * mm, "radius": 558.8 * mm});
            skCircle(sketch, "E85.MirrorC", {"center": v(-4318, -7366) * mm, "radius": 558.8 * mm});
            skCircle(sketch, "E86.MirrorC", {"center": v(-4318, 7366) * mm, "radius": 558.8 * mm});
            skCircle(sketch, "E87.MirrorC", {"center": v(-8382, 2540) * mm, "radius": 558.8 * mm});
            skCircle(sketch, "E88.MirrorC", {"center": v(-8382, -2540) * mm, "radius": 558.8 * mm});
            skSolve(sketch);
        }
        {
            var Q0;
            Q0=qSketchRegion(id+"F20",true);
            extrude(context, id + "F21", {"entities" : qUnion([Q0]), "operationType" : NewBodyOperationType.ADD, "depth" : 1143 * mm});
        }
        {
            var Q0;
            Q0=qCreatedBy(makeId("Top.planeOp"),FACE);
            cPlane(context, id + "F22", {"entities" : qUnion([Q0]), "cplaneType" : CPlaneType.OFFSET, "offset" : 285750 * mm, "width" : 152.4 * mm, "height" : 152.4 * mm});
        }
        {
            var Q0;
            Q0=qCreatedBy(id+"F22.planeOp",FACE);
            var sketch = newSketch(context, id + "F23", { "sketchPlane" : qUnion([Q0])});
            skLineSegment(sketch, "E89.bottom", {"start": v(6350, 4249.42) * mm, "end": v(10160, 4249.42) * mm});
            skLineSegment(sketch, "E89.top", {"start": v(6350, -4249.42) * mm, "end": v(10160, -4249.42) * mm});
            skLineSegment(sketch, "E89.left", {"start": v(6350, 4249.42) * mm, "end": v(6350, -4249.42) * mm});
            skLineSegment(sketch, "E89.right", {"start": v(10160, 4249.42) * mm, "end": v(10160, -4249.42) * mm});
            skLineSegment(sketch, "E90", {"start": v(-11638.26, 0) * mm, "end": v(12105.83, 0) * mm, "construction": true});
            skSolve(sketch);
        }
        {
            var Q0;
            Q0 = qSketchRegion(id + "F23", true);
            extrude(context, id + "F24", {"entities" : qUnion([Q0]), "operationType" : NewBodyOperationType.ADD, "endBound" : BoundingType.SYMMETRIC, "depth" : 508 * mm});
        }
    });
